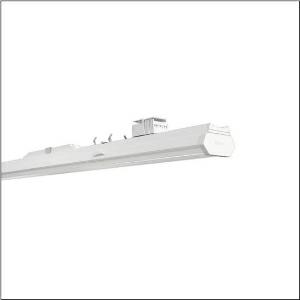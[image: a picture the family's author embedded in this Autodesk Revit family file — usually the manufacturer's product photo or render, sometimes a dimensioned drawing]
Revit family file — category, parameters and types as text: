
# Revit family: licross_11_protected_mo_51td12cn49xg
name_source: partatom
category: Lighting Fixtures
units: mm (PartAtom-declared; Revit-internal decimal feet)

## family parameters
Cut with Voids When Loaded = No
Host = Face
Light Source = No
Part Type = Normal
Room Calculation Point = No
Round Connector Dimension = Use Diameter
Shared = No

## types (1)
- --- (1 x LED, 9070 lm, 49.4 W, 4000K)
    Apparent Load = 49 VA
    CIE Flux Codes = 73 92 98 99 100
    Color Rendering = 80
    Color Temperature = 4000K
    Default Elevation = 1800 mm
    Description = Licross 11 Protected MO, luminaire insert, of sheet steel, galvanised, coil coated, white, length: 1.500mm, width: 90mm, height: 101mm, LED rated luminous flux: 9.070lm, light colour: 840, SDCM (Standard Deviation of Colour Matching)MacAdam ≤ 2 SDCM (initial), control gear: ON/OFF Multilumen, CLOi, with plug, 3-pole, with phase selection, mains connection: 220..240V, AC, 50/60Hz, start of lifetime: 49W, end of service life: 55W, internal wiring halogen-free, primary light control with lens, of plastic, primary optical cover: cover, of PMMA, light emission: direct distribution, primary light characteristic: symmetric, protection rating (complete): IP54, insulation class (complete): insulation class I (protective earthing), certification: CE, ENEC, VDE, UKCA, protection symbol: D if used in an environment with non-conductive dust loads with corresponding accessories, impact resistance: IK06, permissible ambient temperature for indoor applications: -35..+40°C, corresponds to IFS (International Featured Standards) requirements for safety and quality in the food industry, reducing of maximum allowable ambient temperature of 5°C with ceiling mounting, LABS conformity tested according to VDMA 24364:2018-05, The light source and the operating device comply with the requirements of the Ecodesign Regulation (EU) 2019/2020 and are replaceable in accordance with this regulation, packaging unit: 1 piece
    Height = 92 mm
    Lamp = 1 x LED
    Lamp Light Flux = 9070 lm
    Lamp Power = 49.4 W
    Lamp count = 1
    Length = 1500 mm
    Luminous efficacy = 184 lm/W
    Manufacturer = Siteco
    ModVariant = No
    Model = 51TD12CN49XG
    Mounting Place = Ceiling
    Mounting Type = Pendant
    Number of Poles = 1
    OnlyDefault = Yes
    Power Factor = 1
    Product Name = Licross 11 Protected MO
    Product group = luminaire insert | ceiling pendant
    ProductGroupID = 901
    Protection Class = Protection class I
    Protection Degree = IP 54
    RLX_Detail_Level = 1
    RLX_Emergency_Light_Flux = 0 lm
    RLX_Emergency_Type = 0
    RLX_Emergency_Type_DB = No
    RlxData = <blob elided: 22405 chars, md5=7895f892>
    Socket = socket
    Standby Power = 0 W
    System Light Flux = 9070 lm
    System Power = 49 W
    Type Comments = factory setting: luminous flux: 100 % | (A | C | E) | 113 mA
    Type Image = l_1256145.jpg
    URL = http://relux.com
    VarID = @adj_091233
    Voltage = 0 V
    Weight = 0.00 kg
    Width = 88 mm

## geometry (parser evidence)
native form markers: Blend x4, Sweep x10
no freeform markers — native parametric forms only
